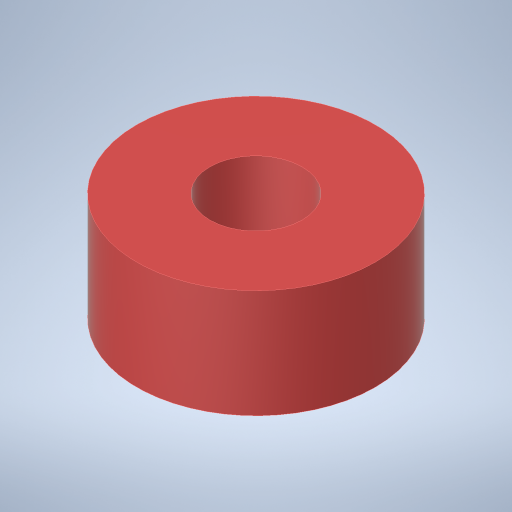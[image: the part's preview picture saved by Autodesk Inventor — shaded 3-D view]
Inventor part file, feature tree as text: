
AUTODESK INVENTOR PART (.ipt)
format: ipt  version: 2023.4 (Build 274418000, 418)  size: 208,384 bytes
history: native  units: in
note: dims shown in document units (in); Inventor stores cm internally (conversion verified against a paired STEP export)
features: sketch x2, extrude x1, hole x1
ambient origin geometry x8: Origin, YZ Plane, XZ Plane, XY Plane, X Axis, Y Axis, Z Axis, Center Point
bodies: Solid1 (feature_tree)
feature tree (4):
  extrude  "Extrusion1"  Depth=0.3125in TaperAngle=0.0deg
  hole  "Hole1"  [1 undecoded]
  sketch  "Sketch1"  dims[d0=0.6875in d1=0.3125in d2=0.0in]
  sketch  "Sketch2"  dims[d3=0.266in d4=0.75in d5=0.507in d6=0.25in d7=0.5635in d8=1.0in d9=0.8108in]
note: 1 required parameter value undecoded (feature->parameter linkage not recoverable at this tier; creation-order binding heuristic only, values carry confidence <= 0.55)
